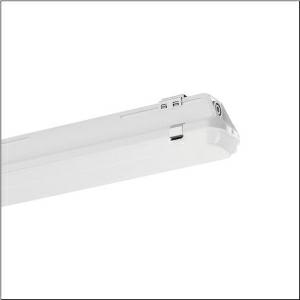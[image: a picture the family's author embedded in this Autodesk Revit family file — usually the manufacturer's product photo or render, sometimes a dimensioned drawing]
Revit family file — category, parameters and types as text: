
# Revit family: monsun_21_emergency_51fb20dp467c3h
name_source: partatom
category: Lighting Fixtures
units: mm (PartAtom-declared; Revit-internal decimal feet)

## family parameters
Cut with Voids When Loaded = No
Host = Face
Light Source = No
Part Type = Normal
Room Calculation Point = No
Round Connector Dimension = Use Diameter
Shared = No

## types (1)
- --- (1 x LED, 5460 lm, 36.5 W, 4000K)
    Apparent Load = 37 VA
    CIE Flux Codes = 45 75 93 94 100
    Color Rendering = 80
    Color Temperature = 4000K
    Default Elevation = 1800 mm
    Description = Monsun 21 emergency, damp-proof luminaire, chain hanger, primary optical cover: enclosure, of PC, light emission: direct distribution, primary light characteristic: symmetric, installation type: vertical mounting, horizontal mounting, surface-mounted, suspended mounting, LED, rated luminous flux: 5.460lm, luminous efficacy: 167lm/W, light colour: 840, colour temperature: 4000K, control gear: DALI 2, with terminal, 5+3-pole, max. 2.5mm², mains connection: 220..240V, AC, 50/60Hz, rated input power: 37W, control gear: single battery element, battery: LiFePO4, 9Ah, housing, of glass-fibre reinforced polyester, uncoated, bright grey, incl. chain hanger, length: 1.590mm, width: 90mm, height: 88mm, clip for enclosure, of stainless steel (V2A), ceiling mounting element, of stainless steel (V2A), chain hanger, of stainless steel (V2A), protection rating (complete): IP66, insulation class (complete): insulation class I (protective earthing), certification: CE, UKCA, protection symbol: D, impact resistance: IK08, permissible operating ambient temperature: +5..+25°C, standard: EN 50419, EN 60598-2-1, EN 60598-2-22, corresponds to IFS (International Featured Standards) requirements for safety and quality in the food industry, for indoor or canopied outdoor use, no direct snow, no direct sun, no direct rain, LABS conformity tested according to VDMA 24364:2018-05, contact your sales advisor before using the luminaires in applications with unclear chemical exposure, large temperature fluctuations or condensation-forming humidity, packaging unit: 1 piece
    Height = 89 mm
    Lamp = 1 x LED
    Lamp Light Flux = 5460 lm
    Lamp Power = 36.5 W
    Lamp count = 1
    Length = 1590 mm
    Luminous efficacy = 150 lm/W
    Manufacturer = Siteco
    ModVariant = No
    Model = 51FB20DP467C3H
    Mounting Place = Ceiling
    Mounting Type = Surface mounted
    Number of Poles = 1
    OnlyDefault = Yes
    Power Factor = 1
    Product Name = Monsun 21 emergency
    Product group = damp-proof luminaire
    ProductGroupID = 300
    Protection Class = Protection class I
    Protection Degree = IP 66
    RLX_Detail_Level = 1
    RLX_Emergency_Light_Flux = 0 lm
    RLX_Emergency_Type = 0
    RLX_Emergency_Type_DB = No
    RlxData = <blob elided: 92529 chars, md5=d334b367>
    Socket = socket
    Standby Power = 0 W
    System Light Flux = 5460 lm
    System Power = 37 W
    Type Comments = : luminous flux: 100 % | dim-lin: 254 | 229 mA
    Type Image = l_1319656.jpg
    URL = http://relux.com
    VarID = @adj_049269
    Voltage = 0 V
    Weight = 0.00 kg
    Width = 90 mm

## geometry (parser evidence)
native form markers: Blend x4, Sweep x14
no freeform markers — native parametric forms only
